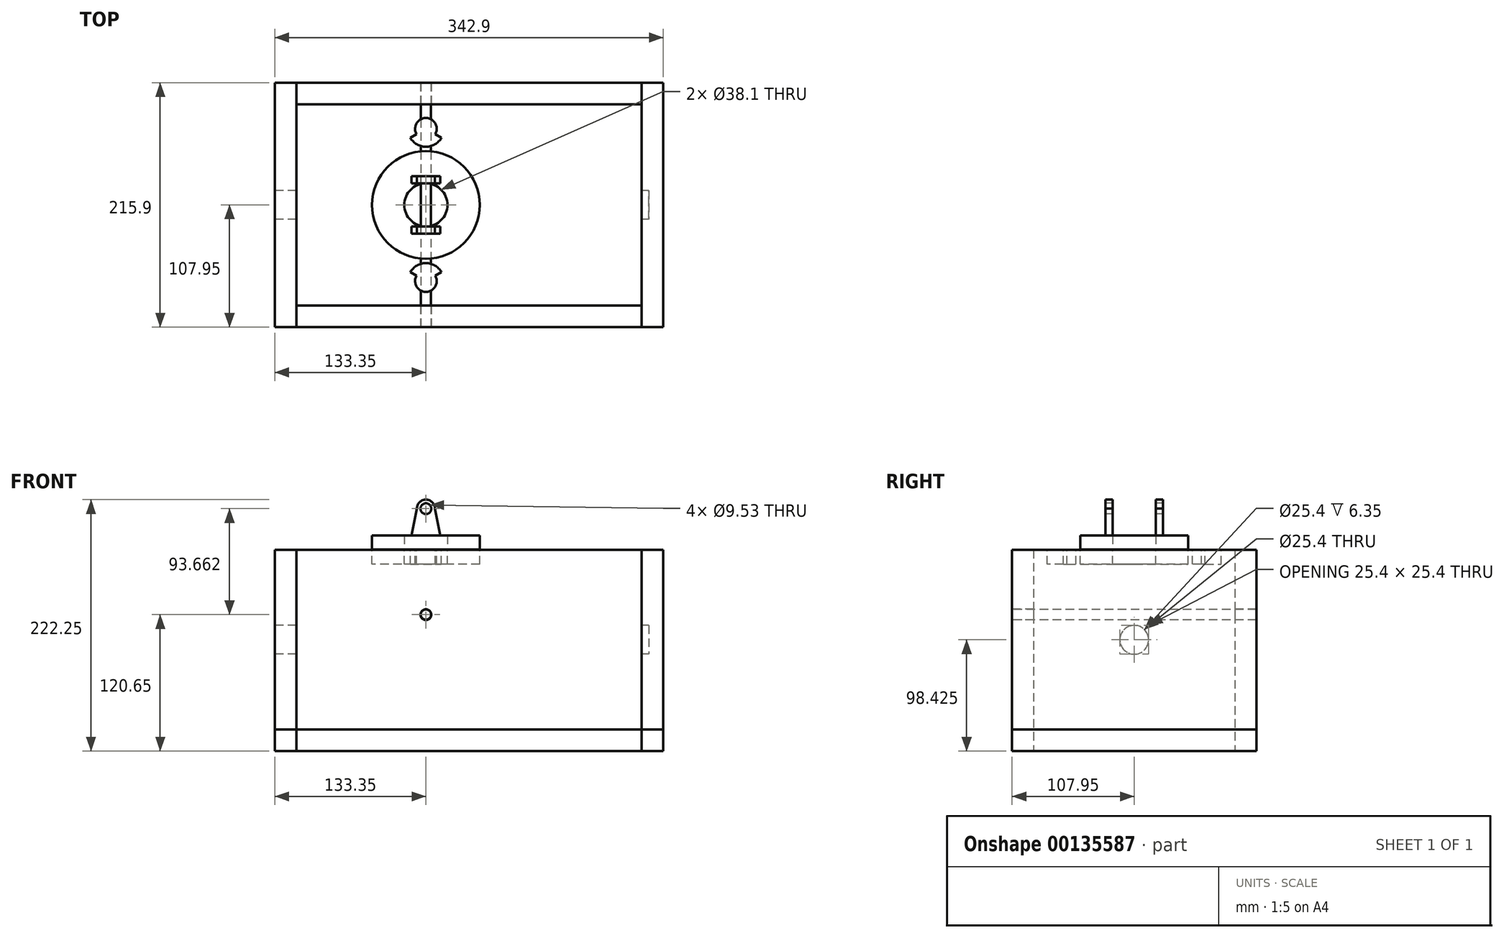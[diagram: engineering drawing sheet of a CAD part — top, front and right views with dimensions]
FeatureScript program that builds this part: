
annotation { "Feature Type Name" : "Feature", "Feature Type Description" : "" }
export const myFeature = defineFeature(function(context is Context, id is Id, definition is map)
    precondition{}
    {
        {
            var Q0;
            Q0=qCreatedBy(makeId("Top.planeOp"),FACE);
            var sketch = newSketch(context, id + "F0", { "sketchPlane" : qUnion([Q0])});
            skLineSegment(sketch, "E0.bottom", {"start": v(-152.4, 88.9) * mm, "end": v(152.4, 88.9) * mm});
            skLineSegment(sketch, "E0.top", {"start": v(-152.4, -88.9) * mm, "end": v(152.4, -88.9) * mm});
            skLineSegment(sketch, "E0.left", {"start": v(-152.4, 88.9) * mm, "end": v(-152.4, -88.9) * mm});
            skLineSegment(sketch, "E0.right", {"start": v(152.4, 88.9) * mm, "end": v(152.4, -88.9) * mm});
            skLineSegment(sketch, "E1.bottom", {"start": v(152.4, 107.95) * mm, "end": v(171.45, 107.95) * mm});
            skLineSegment(sketch, "E1.top", {"start": v(152.4, -107.95) * mm, "end": v(171.45, -107.95) * mm});
            skLineSegment(sketch, "E1.left", {"start": v(152.4, 107.95) * mm, "end": v(152.4, -107.95) * mm});
            skLineSegment(sketch, "E1.right", {"start": v(171.45, 107.95) * mm, "end": v(171.45, -107.95) * mm});
            skLineSegment(sketch, "E2", {"start": v(152.4, 107.95) * mm, "end": v(152.4, 0) * mm});
            skLineSegment(sketch, "E3", {"start": v(152.4, 88.9) * mm, "end": v(152.4, 0) * mm});
            skLineSegment(sketch, "E4.bottom", {"start": v(-171.45, 107.95) * mm, "end": v(-152.4, 107.95) * mm});
            skLineSegment(sketch, "E4.top", {"start": v(-171.45, -107.95) * mm, "end": v(-152.4, -107.95) * mm});
            skLineSegment(sketch, "E4.left", {"start": v(-171.45, 107.95) * mm, "end": v(-171.45, -107.95) * mm});
            skLineSegment(sketch, "E4.right", {"start": v(-152.4, 107.95) * mm, "end": v(-152.4, -107.95) * mm});
            skLineSegment(sketch, "E5", {"start": v(-171.45, 107.95) * mm, "end": v(-171.45, 0) * mm});
            skLineSegment(sketch, "E6", {"start": v(-152.4, 107.95) * mm, "end": v(-152.4, 0) * mm});
            skLineSegment(sketch, "E7", {"start": v(-152.4, 88.9) * mm, "end": v(-152.4, 0) * mm});
            skLineSegment(sketch, "E8.bottom", {"start": v(-152.4, 107.95) * mm, "end": v(152.4, 107.95) * mm});
            skLineSegment(sketch, "E8.left", {"start": v(-152.4, 107.95) * mm, "end": v(-152.4, 88.9) * mm});
            skLineSegment(sketch, "E8.right", {"start": v(152.4, 107.95) * mm, "end": v(152.4, 88.9) * mm});
            skLineSegment(sketch, "E9.bottom", {"start": v(-152.4, -107.95) * mm, "end": v(152.4, -107.95) * mm});
            skLineSegment(sketch, "E9.left", {"start": v(-152.4, -107.95) * mm, "end": v(-152.4, -88.9) * mm});
            skLineSegment(sketch, "E9.right", {"start": v(152.4, -107.95) * mm, "end": v(152.4, -88.9) * mm});
            skLineSegment(sketch, "E10", {"start": v(0, 88.9) * mm, "end": v(0, -88.9) * mm});
            skPoint(sketch, "E11", {"position": v(0, 0) * mm});
            skSolve(sketch);
        }
        {
            var Q0;
            Q0=makeQuery(id+"F0.imprint","IMPRINT",FACE,{"disambiguationData":[TD([[makeQuery(id+"F0.imprint","IMPRINT",EDGE,{"derivedFrom":sQuery(id+"F0.wireOp",EDGE,"E4.bottom")}),-1.0]])]});
            extrude(context, id + "F1", {"entities" : qUnion([Q0]), "depth" : 177.8 * mm});
        }
        {
            var Q0;
            Q0=makeQuery(id+"F0.imprint","IMPRINT",FACE,{"disambiguationData":[TD([[makeQuery(id+"F0.imprint","IMPRINT",EDGE,{"derivedFrom":sQuery(id+"F0.wireOp",EDGE,"E1.bottom")}),-1.0]])]});
            extrude(context, id + "F2", {"entities" : qUnion([Q0]), "depth" : 177.8 * mm});
        }
        {
            var Q0;
            Q0=makeQuery(id+"F0.imprint","IMPRINT",FACE,{"disambiguationData":[TD([[makeQuery(id+"F0.imprint","IMPRINT",EDGE,{"derivedFrom":sQuery(id+"F0.wireOp",EDGE,"E8.bottom")}),-1.0]])]});
            extrude(context, id + "F3", {"entities" : qUnion([Q0]), "depth" : 177.8 * mm});
        }
        {
            var Q0;
            Q0=makeQuery(id+"F0.imprint","IMPRINT",FACE,{"disambiguationData":[TD([[makeQuery(id+"F0.imprint","IMPRINT",EDGE,{"derivedFrom":sQuery(id+"F0.wireOp",EDGE,"E9.bottom")}),1.0]])]});
            extrude(context, id + "F4", {"entities" : qUnion([Q0]), "depth" : 177.8 * mm});
        }
        {
            var Q0;
            Q0=qCreatedBy(makeId("Top.planeOp"),FACE);
            var sketch = newSketch(context, id + "F5", { "sketchPlane" : qUnion([Q0])});
            skLineSegment(sketch, "E12.bottom", {"start": v(-171.45, -107.95) * mm, "end": v(171.45, -107.95) * mm});
            skLineSegment(sketch, "E12.top", {"start": v(-171.45, 107.95) * mm, "end": v(171.45, 107.95) * mm});
            skLineSegment(sketch, "E12.left", {"start": v(-171.45, -107.95) * mm, "end": v(-171.45, 107.95) * mm});
            skLineSegment(sketch, "E12.right", {"start": v(171.45, -107.95) * mm, "end": v(171.45, 107.95) * mm});
            skSolve(sketch);
        }
        {
            var Q0;
            Q0=qSketchRegion(id+"F5",true);
            extrude(context, id + "F6", {"entities" : qUnion([Q0]), "depth" : 19.05 * mm});
        }
        {
            var Q0;
            Q0=makeQuery(id+"F1.opExtrude","SWEPT_FACE",FACE,{"disambiguationData":[OSD([sQuery(id+"F0.wireOp",EDGE,"E4.left"),sQuery(id+"F0.wireOp",EDGE,"E5")])]});
            var sketch = newSketch(context, id + "F7", { "sketchPlane" : qUnion([Q0])});
            skPoint(sketch, "E13", {"position": v(0, 177.8) * mm});
            skPoint(sketch, "E14", {"position": v(0, 19.05) * mm});
            skLineSegment(sketch, "E15", {"start": v(0, 177.8) * mm, "end": v(0, 19.05) * mm, "construction": true});
            skPoint(sketch, "E16", {"position": v(0, 98.43) * mm});
            skCircle(sketch, "E17", {"center": v(0, 98.43) * mm, "radius": 12.7 * mm});
            skSolve(sketch);
        }
        {
            var Q0;
            Q0=makeQuery(id+"F7.imprint","IMPRINT",FACE,{"disambiguationData":[TD([[makeQuery(id+"F7.imprint","IMPRINT",EDGE,{"derivedFrom":sQuery(id+"F7.wireOp",EDGE,"E17")}),1.0]])]});
            var Q1;
            Q1=sQuery(id+"F7.wireOp",EDGE,"E17");
            extrude(context, id + "F8", {"entities" : qUnion([Q0]), "operationType" : NewBodyOperationType.REMOVE, "surfaceEntities" : qUnion([Q1]), "oppositeDirection" : true, "depth" : 330.2 * mm});
        }
        {
            var Q0;
            Q0=makeQuery(id+"F1.opExtrude","SWEPT_FACE",FACE,{"disambiguationData":[OSD([sQuery(id+"F0.wireOp",EDGE,"E4.left"),sQuery(id+"F0.wireOp",EDGE,"E5")])]});
            var sketch = newSketch(context, id + "F9", { "sketchPlane" : qUnion([Q0])});
            skCircle(sketch, "E18", {"center": v(0, 98.43) * mm, "radius": 12.38 * mm});
            skSolve(sketch);
        }
        {
            var Q0;
            Q0=makeQuery(id+"F1.opExtrude","CAP_FACE",FACE,{"disambiguationData":[OSD([sQuery(id+"F0.wireOp",EDGE,"E4.bottom"),sQuery(id+"F0.wireOp",EDGE,"E4.top"),sQuery(id+"F0.wireOp",EDGE,"E4.left"),sQuery(id+"F0.wireOp",EDGE,"E4.right"),sQuery(id+"F0.wireOp",EDGE,"E5"),sQuery(id+"F0.wireOp",EDGE,"E7"),sQuery(id+"F0.wireOp",EDGE,"E8.left"),sQuery(id+"F0.wireOp",EDGE,"E9.left")])],"isStart":false});
            var sketch = newSketch(context, id + "F10", { "sketchPlane" : qUnion([Q0])});
            skLineSegment(sketch, "E19", {"start": v(-152.4, 0) * mm, "end": v(152.4, 0) * mm, "construction": true});
            skPoint(sketch, "E19.endSnap0", {"position": v(-152.4, 0) * mm});
            skLineSegment(sketch, "E20", {"start": v(-152.4, 0) * mm, "end": v(-38.1, 0) * mm, "construction": true});
            skCircle(sketch, "E21", {"center": v(-38.1, 0) * mm, "radius": 47.63 * mm});
            skCircle(sketch, "E22", {"center": v(-38.1, 0) * mm, "radius": 19.05 * mm});
            skLineSegment(sketch, "E23", {"start": v(-38.1, 0) * mm, "end": v(-38.1, -107.95) * mm, "construction": true});
            skSolve(sketch);
        }
        {
            var Q0;
            Q0=qSketchRegion(id+"F10",true);
            extrude(context, id + "F11", {"entities" : qUnion([Q0]), "oppositeDirection" : true, "depth" : 12.7 * mm});
        }
        {
            var Q0;
            Q0=makeQuery(id+"F4.opExtrude","SWEPT_FACE",FACE,{"disambiguationData":[OSD([sQuery(id+"F0.wireOp",EDGE,"E9.bottom")])]});
            var sketch = newSketch(context, id + "F12", { "sketchPlane" : qUnion([Q0])});
            skLineSegment(sketch, "E24", {"start": v(-152.4, 88.9) * mm, "end": v(-38.1, 88.9) * mm, "construction": true});
            skLineSegment(sketch, "E25", {"start": v(-38.1, 88.9) * mm, "end": v(152.4, 88.9) * mm, "construction": true});
            skLineSegment(sketch, "E26", {"start": v(-38.1, 88.9) * mm, "end": v(-38.1, 120.65) * mm, "construction": true});
            skCircle(sketch, "E27", {"center": v(-38.1, 120.65) * mm, "radius": 4.76 * mm});
            skSolve(sketch);
        }
        {
            var Q0;
            Q0=makeQuery(id+"F12.imprint","IMPRINT",FACE,{"disambiguationData":[TD([[makeQuery(id+"F12.imprint","IMPRINT",EDGE,{"derivedFrom":sQuery(id+"F12.wireOp",EDGE,"E27")}),1.0]])]});
            var Q1;
            Q1=sQuery(id+"F12.wireOp",EDGE,"E27");
            extrude(context, id + "F13", {"entities" : qUnion([Q0]), "operationType" : NewBodyOperationType.REMOVE, "surfaceEntities" : qUnion([Q1]), "oppositeDirection" : true, "depth" : 206.38 * mm});
        }
        {
            var Q0;
            Q0=makeQuery(id+"F3.opExtrude","SWEPT_FACE",FACE,{"disambiguationData":[OSD([sQuery(id+"F0.wireOp",EDGE,"E8.bottom")])]});
            var sketch = newSketch(context, id + "F14", { "sketchPlane" : qUnion([Q0])});
            skLineSegment(sketch, "E28.0.0", {"start": v(-152.4, 0) * mm, "end": v(152.4, 0) * mm});
            skLineSegment(sketch, "E28.0.1", {"start": v(152.4, 0) * mm, "end": v(152.4, 177.8) * mm});
            skLineSegment(sketch, "E28.0.2", {"start": v(152.4, 177.8) * mm, "end": v(-152.4, 177.8) * mm});
            skLineSegment(sketch, "E28.0.3", {"start": v(-152.4, 177.8) * mm, "end": v(-152.4, 0) * mm});
            skCircle(sketch, "E29.0", {"center": v(38.1, 120.65) * mm, "radius": 4.76 * mm});
            skSolve(sketch);
        }
        {
            var Q0;
            Q0=makeQuery(id+"F14.imprint","IMPRINT",FACE,{"disambiguationData":[TD([[makeQuery(id+"F14.imprint","IMPRINT",EDGE,{"derivedFrom":sQuery(id+"F14.wireOp",EDGE,"E29.0")}),1.0]])]});
            var Q1;
            Q1=sQuery(id+"F14.wireOp",EDGE,"E29.0");
            extrude(context, id + "F15", {"entities" : qUnion([Q0]), "operationType" : NewBodyOperationType.REMOVE, "surfaceEntities" : qUnion([Q1]), "oppositeDirection" : true, "depth" : 25.4 * mm});
        }
        {
            var Q0;
            Q0=makeQuery(id+"F4.opExtrude","SWEPT_FACE",FACE,{"disambiguationData":[OSD([sQuery(id+"F0.wireOp",EDGE,"E9.bottom")])]});
            var sketch = newSketch(context, id + "F16", { "sketchPlane" : qUnion([Q0])});
            skCircle(sketch, "E30.0", {"center": v(-38.1, 120.65) * mm, "radius": 4.76 * mm});
            skCircle(sketch, "E31", {"center": v(-38.1, 120.65) * mm, "radius": 4.5 * mm});
            skSolve(sketch);
        }
        {
            var Q0;
            Q0=makeQuery(id+"F16.imprint","IMPRINT",FACE,{"disambiguationData":[TD([[makeQuery(id+"F16.imprint","IMPRINT",EDGE,{"derivedFrom":sQuery(id+"F16.wireOp",EDGE,"E31")}),1.0]])]});
            extrude(context, id + "F17", {"entities" : qUnion([Q0]), "oppositeDirection" : true, "depth" : 215.9 * mm});
        }
        {
            var Q0;
            Q0=makeQuery(id+"F10.imprint","IMPRINT",FACE,{"disambiguationData":[TD([[makeQuery(id+"F10.imprint","IMPRINT",EDGE,{"derivedFrom":makeQuery(id+"F1.opExtrude","CAP_EDGE",EDGE,{"disambiguationData":[OSD([sQuery(id+"F0.wireOp",EDGE,"E4.bottom")])],"isStart":false})}),-1.0]])]});
            var sketch = newSketch(context, id + "F18", { "sketchPlane" : qUnion([Q0])});
            skLineSegment(sketch, "E32", {"start": v(0, 0) * mm, "end": v(-38.1, 0) * mm, "construction": true});
            skLineSegment(sketch, "E33", {"start": v(-38.1, 0) * mm, "end": v(-38.1, 67.31) * mm, "construction": true});
            skArc(sketch, "E34", {"start": v(-51.85, 59.37) * mm, "mid": v(-38.1, 51.44) * mm, "end": v(-24.35, 59.37) * mm});
            skLineSegment(sketch, "E35", {"start": v(-38.1, 51.44) * mm, "end": v(-38.1, 83.19) * mm, "construction": true});
            skLineSegment(sketch, "E36", {"start": v(-53.98, 67.31) * mm, "end": v(-22.23, 67.31) * mm, "construction": true});
            skLineSegment(sketch, "E37", {"start": v(-46.35, 62.55) * mm, "end": v(-51.85, 59.37) * mm});
            skLineSegment(sketch, "E38", {"start": v(-29.85, 62.55) * mm, "end": v(-24.35, 59.37) * mm});
            skArc(sketch, "E39", {"start": v(-29.85, 62.55) * mm, "mid": v(-38.1, 76.84) * mm, "end": v(-46.35, 62.55) * mm});
            skSolve(sketch);
        }
        {
            var Q0;
            Q0=qSketchRegion(id+"F18",true);
            extrude(context, id + "F19", {"entities" : qUnion([Q0]), "oppositeDirection" : true, "depth" : 12.7 * mm});
        }
        {
            var Q0;
            Q0=makeQuery(id+"F19.opExtrude","SWEPT_BODY",BODY,{"disambiguationData":[OSD([sQuery(id+"F18.wireOp",EDGE,"E34"),sQuery(id+"F18.wireOp",EDGE,"E37"),sQuery(id+"F18.wireOp",EDGE,"E38"),sQuery(id+"F18.wireOp",EDGE,"E39")])]});
            var Q1;
            Q1=qCreatedBy(makeId("Front.planeOp"),FACE);
            mirror(context, id + "F20", {"entities" : qUnion([Q0]), "mirrorPlane" : qUnion([Q1])});
        }
        {
            var Q0;
            Q0=makeQuery(id+"F10.imprint","IMPRINT",FACE,{"disambiguationData":[TD([[makeQuery(id+"F10.imprint","IMPRINT",EDGE,{"derivedFrom":sQuery(id+"F10.wireOp",EDGE,"E21")}),1.0]])]});
            extrude(context, id + "F21", {"entities" : qUnion([Q0]), "depth" : 12.7 * mm, "hasSecondDirection" : true, "secondDirectionOppositeDirection" : false, "secondDirectionDepth" : 0.5 * mm});
        }
        {
            var Q0;
            Q0=makeQuery(id+"F21.opExtrude","CAP_FACE",FACE,{"disambiguationData":[OSD([sQuery(id+"F10.wireOp",EDGE,"E21"),sQuery(id+"F10.wireOp",EDGE,"E22")])],"isStart":false});
            var sketch = newSketch(context, id + "F22", { "sketchPlane" : qUnion([Q0])});
            skLineSegment(sketch, "E40", {"start": v(-57.15, 0) * mm, "end": v(-19.05, 0) * mm, "construction": true});
            skLineSegment(sketch, "E41", {"start": v(-38.1, 0) * mm, "end": v(-38.1, 19.05) * mm, "construction": true});
            skLineSegment(sketch, "E42", {"start": v(-38.1, 0) * mm, "end": v(-38.1, -19.05) * mm, "construction": true});
            skLineSegment(sketch, "E43", {"start": v(-38.1, 19.05) * mm, "end": v(-25.4, 19.05) * mm, "construction": true});
            skLineSegment(sketch, "E44", {"start": v(-38.1, 19.05) * mm, "end": v(-50.8, 19.05) * mm, "construction": true});
            skLineSegment(sketch, "E45.bottom", {"start": v(-50.8, 19.05) * mm, "end": v(-25.4, 19.05) * mm});
            skLineSegment(sketch, "E45.top", {"start": v(-50.8, 25.4) * mm, "end": v(-25.4, 25.4) * mm});
            skLineSegment(sketch, "E45.left", {"start": v(-50.8, 19.05) * mm, "end": v(-50.8, 25.4) * mm});
            skLineSegment(sketch, "E45.right", {"start": v(-25.4, 19.05) * mm, "end": v(-25.4, 25.4) * mm});
            skLineSegment(sketch, "E46.MirrorCS", {"start": v(-38.1, -19.05) * mm, "end": v(-25.4, -19.05) * mm, "construction": true});
            skLineSegment(sketch, "E47.MirrorCS", {"start": v(-38.1, -19.05) * mm, "end": v(-50.8, -19.05) * mm, "construction": true});
            skLineSegment(sketch, "E48.MirrorCS", {"start": v(-25.4, -19.05) * mm, "end": v(-25.4, -25.4) * mm});
            skLineSegment(sketch, "E49.MirrorCS", {"start": v(-50.8, -19.05) * mm, "end": v(-50.8, -25.4) * mm});
            skLineSegment(sketch, "E50.MirrorCS", {"start": v(-50.8, -25.4) * mm, "end": v(-25.4, -25.4) * mm});
            skLineSegment(sketch, "E51", {"start": v(-50.8, -19.05) * mm, "end": v(-25.4, -19.05) * mm});
            skSolve(sketch);
        }
        {
            var Q0;
            Q0=qSketchRegion(id+"F22",true);
            extrude(context, id + "F23", {"entities" : qUnion([Q0]), "operationType" : NewBodyOperationType.ADD, "depth" : 31.75 * mm});
        }
        {
            var Q0;
            Q0=makeQuery(id+"F23.opExtrude","SWEPT_FACE",FACE,{"disambiguationData":[OSD([sQuery(id+"F22.wireOp",EDGE,"E50.MirrorCS")])]});
            var sketch = newSketch(context, id + "F24", { "sketchPlane" : qUnion([Q0])});
            skLineSegment(sketch, "E52", {"start": v(-47.62, 206.38) * mm, "end": v(-28.57, 206.38) * mm, "construction": true});
            skLineSegment(sketch, "E53", {"start": v(-38.1, 222.25) * mm, "end": v(-38.1, 206.38) * mm, "construction": true});
            skLineSegment(sketch, "E54", {"start": v(-38.1, 206.38) * mm, "end": v(-38.1, 214.31) * mm, "construction": true});
            skArc(sketch, "E55", {"start": v(-30.16, 214.31) * mm, "mid": v(-38.1, 222.25) * mm, "end": v(-46.04, 214.31) * mm});
            skLineSegment(sketch, "E56", {"start": v(-38.1, 214.31) * mm, "end": v(-30.16, 214.31) * mm, "construction": true});
            skLineSegment(sketch, "E57", {"start": v(-38.1, 214.31) * mm, "end": v(-46.04, 214.31) * mm, "construction": true});
            skLineSegment(sketch, "E58", {"start": v(-46.04, 214.31) * mm, "end": v(-50.8, 190.5) * mm});
            skLineSegment(sketch, "E59", {"start": v(-30.16, 214.31) * mm, "end": v(-25.4, 190.5) * mm});
            skPoint(sketch, "E60.orphan", {"position": v(-25.4, 206.38) * mm});
            skPoint(sketch, "E61.orphan", {"position": v(-50.8, 206.38) * mm});
            skCircle(sketch, "E62", {"center": v(-38.1, 214.31) * mm, "radius": 4.76 * mm});
            skSolve(sketch);
        }
        {
            var Q0;
            {var subQ0=sQuery(id+"F24.wireOp",EDGE,"E59");Q0=makeQuery(id+"F24.imprint","IMPRINT",FACE,{"disambiguationData":[TD([[makeQuery(id+"F24.imprint","IMPRINT",EDGE,{"derivedFrom":subQ0}),1.0]])]});}
            var Q1;
            Q1=makeQuery(id+"F24.imprint","IMPRINT",FACE,{"disambiguationData":[TD([[makeQuery(id+"F24.imprint","IMPRINT",EDGE,{"derivedFrom":sQuery(id+"F24.wireOp",EDGE,"E62")}),1.0]])]});
            var Q2;
            {var subQ0=sQuery(id+"F24.wireOp",EDGE,"E58");Q2=makeQuery(id+"F24.imprint","IMPRINT",FACE,{"disambiguationData":[TD([[makeQuery(id+"F24.imprint","IMPRINT",EDGE,{"derivedFrom":subQ0}),-1.0]])]});}
            extrude(context, id + "F25", {"entities" : qUnion([Q0, Q1, Q2]), "operationType" : NewBodyOperationType.REMOVE, "oppositeDirection" : true, "depth" : 127 * mm});
        }
    });
